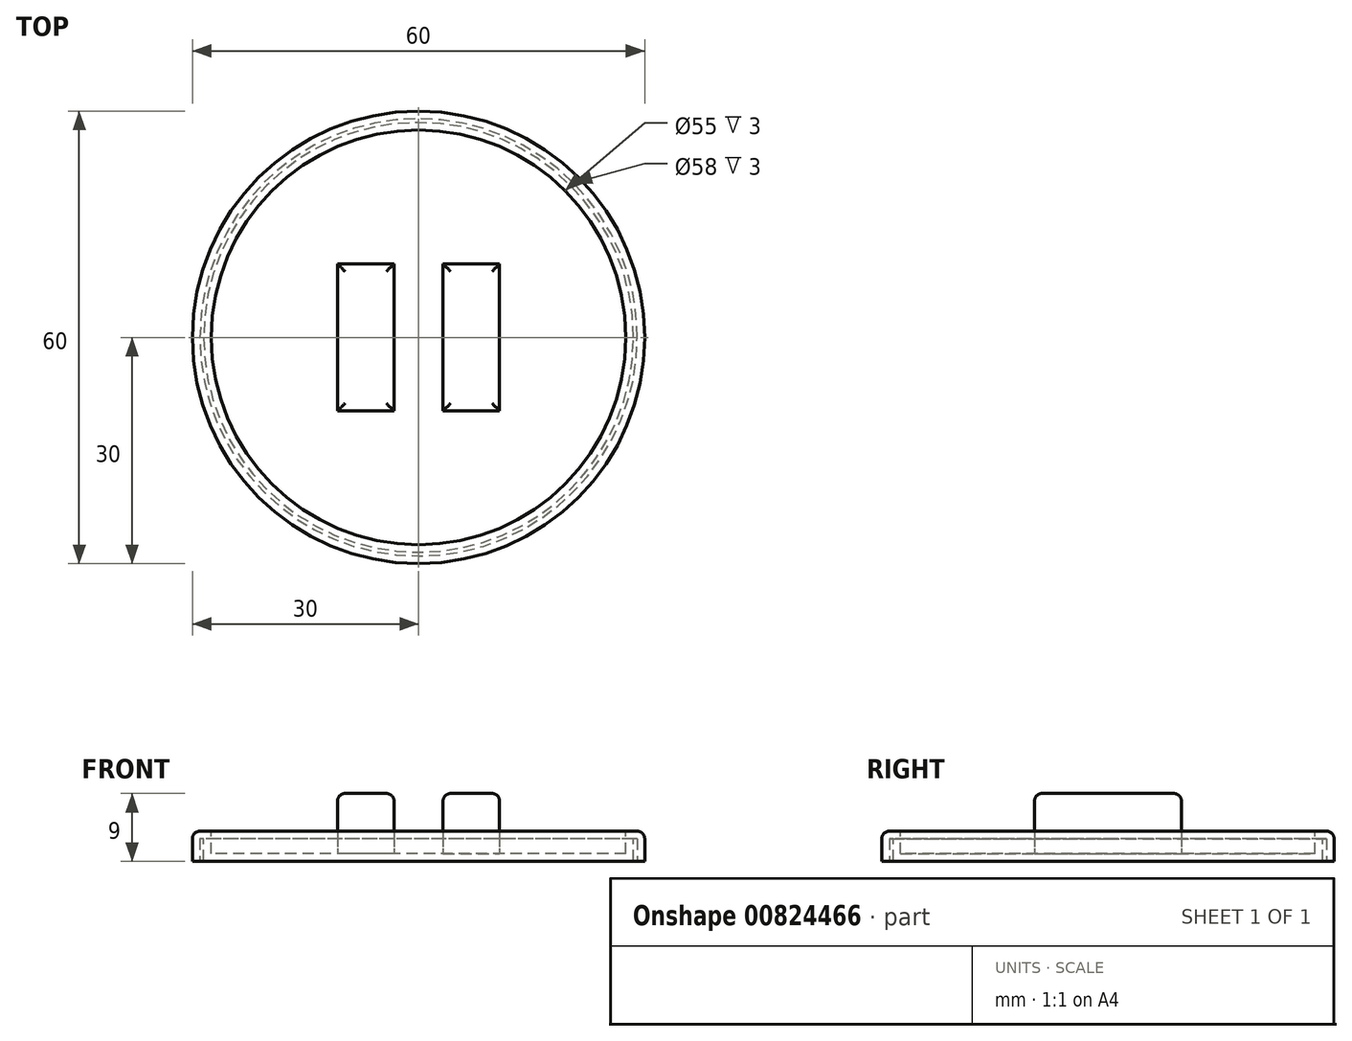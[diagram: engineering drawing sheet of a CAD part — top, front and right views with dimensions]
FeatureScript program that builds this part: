
annotation { "Feature Type Name" : "Feature", "Feature Type Description" : "" }
export const myFeature = defineFeature(function(context is Context, id is Id, definition is map)
    precondition{}
    {
        {
            var Q0;
            Q0=qCreatedBy(makeId("Top.planeOp"),FACE);
            var sketch = newSketch(context, id + "F0", { "sketchPlane" : qUnion([Q0])});
            skCircle(sketch, "E0", {"center": v(0, 0) * mm, "radius": 30 * mm});
            skSolve(sketch);
        }
        {
            var Q0;
            Q0 = qSketchRegion(id + "F0", true);
            extrude(context, id + "F1", {"entities" : qUnion([Q0]), "depth" : 4 * mm, "offsetDistance" : 25 * mm});
        }
        {
            var Q0;
            Q0=makeQuery(id+"F1.opExtrude","CAP_FACE",FACE,{"disambiguationData":[OSD([sQuery(id+"F0.wireOp",EDGE,"E0")])],"isStart":false});
            var sketch = newSketch(context, id + "F2", { "sketchPlane" : qUnion([Q0])});
            skCircle(sketch, "E1", {"center": v(0, 0) * mm, "radius": 27.5 * mm});
            skSolve(sketch);
        }
        {
            var Q0;
            Q0 = qSketchRegion(id + "F2", true);
            extrude(context, id + "F3", {"entities" : qUnion([Q0]), "operationType" : NewBodyOperationType.REMOVE, "oppositeDirection" : true, "depth" : 3 * mm, "offsetDistance" : 25 * mm});
        }
        {
            var Q0;
            Q0=makeQuery(id+"F1.opExtrude","CAP_EDGE",EDGE,{"disambiguationData":[OSD([sQuery(id+"F0.wireOp",EDGE,"E0")])],"isStart":false});
            fillet(context, id + "F4", {"entities" : qUnion([Q0]), "radius" : 1 * mm, "tangentPropagation" : true, "allowEdgeOverflow" : false});
        }
        {
            var Q0;
            Q0=makeQuery(id+"F1.opExtrude","CAP_FACE",FACE,{"disambiguationData":[OSD([sQuery(id+"F0.wireOp",EDGE,"E0")])],"isStart":true});
            shell(context, id + "F5", {"entities" : qUnion([Q0]), "thickness" : 1 * mm});
        }
        {
            var Q0;
            Q0=makeQuery(id+"F3.boolean.opBoolean","COPY",FACE,{"derivedFrom":makeQuery(id+"F3.opExtrude","CAP_FACE",FACE,{"disambiguationData":[OSD([sQuery(id+"F2.wireOp",EDGE,"E1")])],"isStart":false})});
            var sketch = newSketch(context, id + "F6", { "sketchPlane" : qUnion([Q0])});
            skLineSegment(sketch, "E2.bottom", {"start": v(3.25, -9.75) * mm, "end": v(10.75, -9.75) * mm});
            skLineSegment(sketch, "E2.top", {"start": v(3.25, 9.75) * mm, "end": v(10.75, 9.75) * mm});
            skLineSegment(sketch, "E2.left", {"start": v(3.25, -9.75) * mm, "end": v(3.25, 9.75) * mm});
            skLineSegment(sketch, "E2.right", {"start": v(10.75, -9.75) * mm, "end": v(10.75, 9.75) * mm});
            skLineSegment(sketch, "E3.bottom", {"start": v(-3.25, -9.75) * mm, "end": v(-10.75, -9.75) * mm});
            skLineSegment(sketch, "E3.top", {"start": v(-3.25, 9.75) * mm, "end": v(-10.75, 9.75) * mm});
            skLineSegment(sketch, "E3.left", {"start": v(-3.25, -9.75) * mm, "end": v(-3.25, 9.75) * mm});
            skLineSegment(sketch, "E3.right", {"start": v(-10.75, -9.75) * mm, "end": v(-10.75, 9.75) * mm});
            skSolve(sketch);
        }
        {
            var Q0;
            Q0 = qSketchRegion(id + "F6", true);
            extrude(context, id + "F7", {"entities" : qUnion([Q0]), "operationType" : NewBodyOperationType.ADD, "depth" : 8 * mm, "offsetDistance" : 25 * mm});
        }
        {
            var Q0;
            Q0=makeQuery(id+"F7.opExtrude","CAP_FACE",FACE,{"disambiguationData":[OSD([sQuery(id+"F6.wireOp",EDGE,"E2.bottom"),sQuery(id+"F6.wireOp",EDGE,"E2.top"),sQuery(id+"F6.wireOp",EDGE,"E2.left"),sQuery(id+"F6.wireOp",EDGE,"E2.right")])],"isStart":false});
            var Q1;
            Q1=makeQuery(id+"F7.opExtrude","CAP_FACE",FACE,{"disambiguationData":[OSD([sQuery(id+"F6.wireOp",EDGE,"E3.bottom"),sQuery(id+"F6.wireOp",EDGE,"E3.top"),sQuery(id+"F6.wireOp",EDGE,"E3.left"),sQuery(id+"F6.wireOp",EDGE,"E3.right")])],"isStart":false});
            fillet(context, id + "F8", {"entities" : qUnion([Q0, Q1]), "radius" : 1 * mm, "tangentPropagation" : true, "allowEdgeOverflow" : false});
        }
    });
